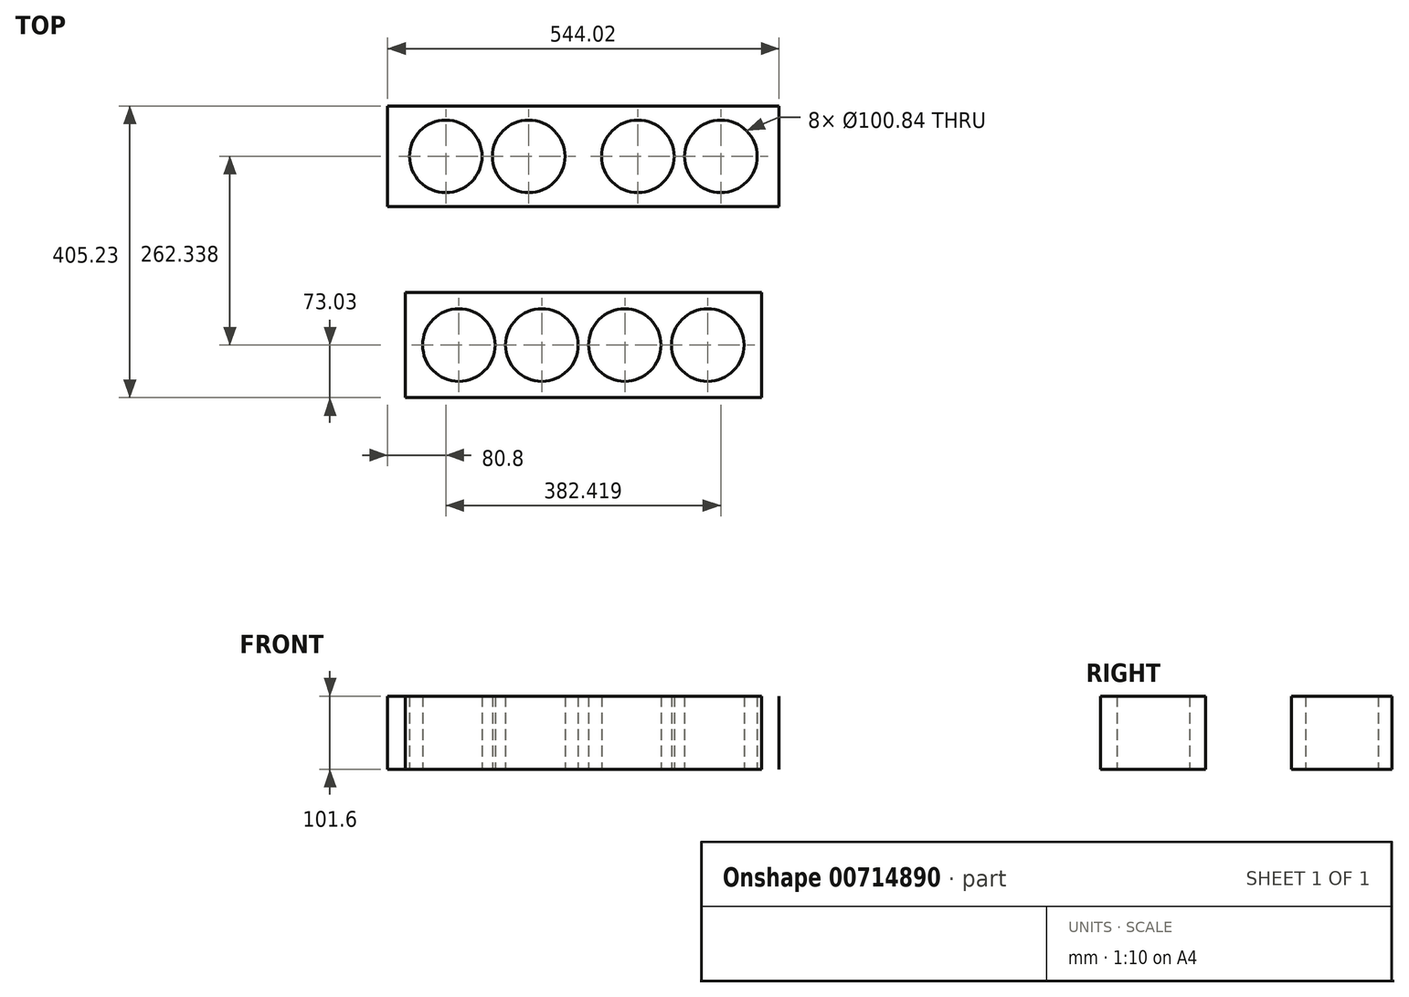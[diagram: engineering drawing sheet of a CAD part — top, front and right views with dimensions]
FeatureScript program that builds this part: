
annotation { "Feature Type Name" : "Feature", "Feature Type Description" : "" }
export const myFeature = defineFeature(function(context is Context, id is Id, definition is map)
    precondition{}
    {
        {
            var Q0;
            Q0=qCreatedBy(makeId("Top.planeOp"),FACE);
            var sketch = newSketch(context, id + "F0", { "sketchPlane" : qUnion([Q0])});
            skCircle(sketch, "E0", {"center": v(-220.21, 0) * mm, "radius": 50.42 * mm});
            skCircle(sketch, "E1.1.0.0", {"center": v(-104.9, 0) * mm, "radius": 50.42 * mm});
            skCircle(sketch, "E1.2.0.0", {"center": v(10.42, 0) * mm, "radius": 50.42 * mm});
            skCircle(sketch, "E1.3.0.0", {"center": v(125.73, 0) * mm, "radius": 50.42 * mm});
            skLineSegment(sketch, "E1.direction1", {"start": v(-220.21, 0) * mm, "end": v(-104.9, 0) * mm, "construction": true});
            skLineSegment(sketch, "E2", {"start": v(-220.21, 0) * mm, "end": v(125.73, 0) * mm, "construction": true});
            skLineSegment(sketch, "E3.bottom", {"start": v(200.4, 73.02) * mm, "end": v(-294.9, 73.03) * mm});
            skLineSegment(sketch, "E3.top", {"start": v(200.4, -73.03) * mm, "end": v(-294.9, -73.02) * mm});
            skLineSegment(sketch, "E3.left", {"start": v(200.4, 73.02) * mm, "end": v(200.4, -73.03) * mm});
            skLineSegment(sketch, "E3.right", {"start": v(-294.9, 73.03) * mm, "end": v(-294.9, -73.02) * mm});
            skPoint(sketch, "E3.middle", {"position": v(-47.24, 0) * mm});
            skLineSegment(sketch, "E4.MirrorCS", {"start": v(-238.45, 262.34) * mm, "end": v(-123.13, 262.34) * mm, "construction": true});
            skLineSegment(sketch, "E5.MirrorCS", {"start": v(-319.25, 192.46) * mm, "end": v(-319.25, 332.2) * mm});
            skLineSegment(sketch, "E6.MirrorCS", {"start": v(224.77, 192.5) * mm, "end": v(224.77, 332.2) * mm});
            skLineSegment(sketch, "E7.MirrorCS", {"start": v(224.77, 332.2) * mm, "end": v(-319.25, 332.2) * mm});
            skCircle(sketch, "E8.MirrorC", {"center": v(-238.45, 262.34) * mm, "radius": 50.42 * mm});
            skCircle(sketch, "E9.MirrorC", {"center": v(-123.13, 262.34) * mm, "radius": 50.42 * mm});
            skCircle(sketch, "E10.MirrorC", {"center": v(28.65, 262.34) * mm, "radius": 50.42 * mm});
            skCircle(sketch, "E11.MirrorC", {"center": v(143.97, 262.34) * mm, "radius": 50.42 * mm});
            skPoint(sketch, "E12.MirrorP", {"position": v(-47.24, 262.34) * mm});
            skLineSegment(sketch, "E13.MirrorCS", {"start": v(-238.45, 262.34) * mm, "end": v(143.97, 262.34) * mm, "construction": true});
            skLineSegment(sketch, "E14.MirrorCS", {"start": v(224.77, 192.5) * mm, "end": v(-319.25, 192.46) * mm});
            skLineSegment(sketch, "E15", {"start": v(125.73, 0) * mm, "end": v(125.73, 367.3) * mm, "construction": true});
            skLineSegment(sketch, "E16", {"start": v(-220.21, 0) * mm, "end": v(-220.21, 411.55) * mm, "construction": true});
            skLineSegment(sketch, "E17", {"start": v(-47.24, 332.2) * mm, "end": v(-47.24, 192.48) * mm, "construction": true});
            skLineSegment(sketch, "E18", {"start": v(-47.24, 0) * mm, "end": v(-47.24, 332.2) * mm, "construction": true});
            skSolve(sketch);
        }
        {
            var Q0;
            {var subQ1=sQuery(id+"F0.wireOp",EDGE,"E5.MirrorCS");Q0=makeQuery(id+"F0.imprint","IMPRINT",FACE,{"disambiguationData":[TD([[makeQuery(id+"F0.imprint","IMPRINT",EDGE,{"derivedFrom":subQ1}),-1.0]])]});}
            var Q1;
            {var subQ1=sQuery(id+"F0.wireOp",EDGE,"E6.MirrorCS");Q1=makeQuery(id+"F0.imprint","IMPRINT",FACE,{"disambiguationData":[TD([[makeQuery(id+"F0.imprint","IMPRINT",EDGE,{"derivedFrom":subQ1}),1.0]])]});}
            extrude(context, id + "F1", {"entities" : qUnion([Q0, Q1]), "depth" : 101.6 * mm, "offsetDistance" : 25.4 * mm});
        }
        {
            var Q0;
            Q0=makeQuery(id+"F0.imprint","IMPRINT",FACE,{"disambiguationData":[TD([[makeQuery(id+"F0.imprint","IMPRINT",EDGE,{"derivedFrom":sQuery(id+"F0.wireOp",EDGE,"E0")}),-1.0]])]});
            extrude(context, id + "F2", {"entities" : qUnion([Q0]), "depth" : 101.6 * mm, "offsetDistance" : 25.4 * mm});
        }
    });
